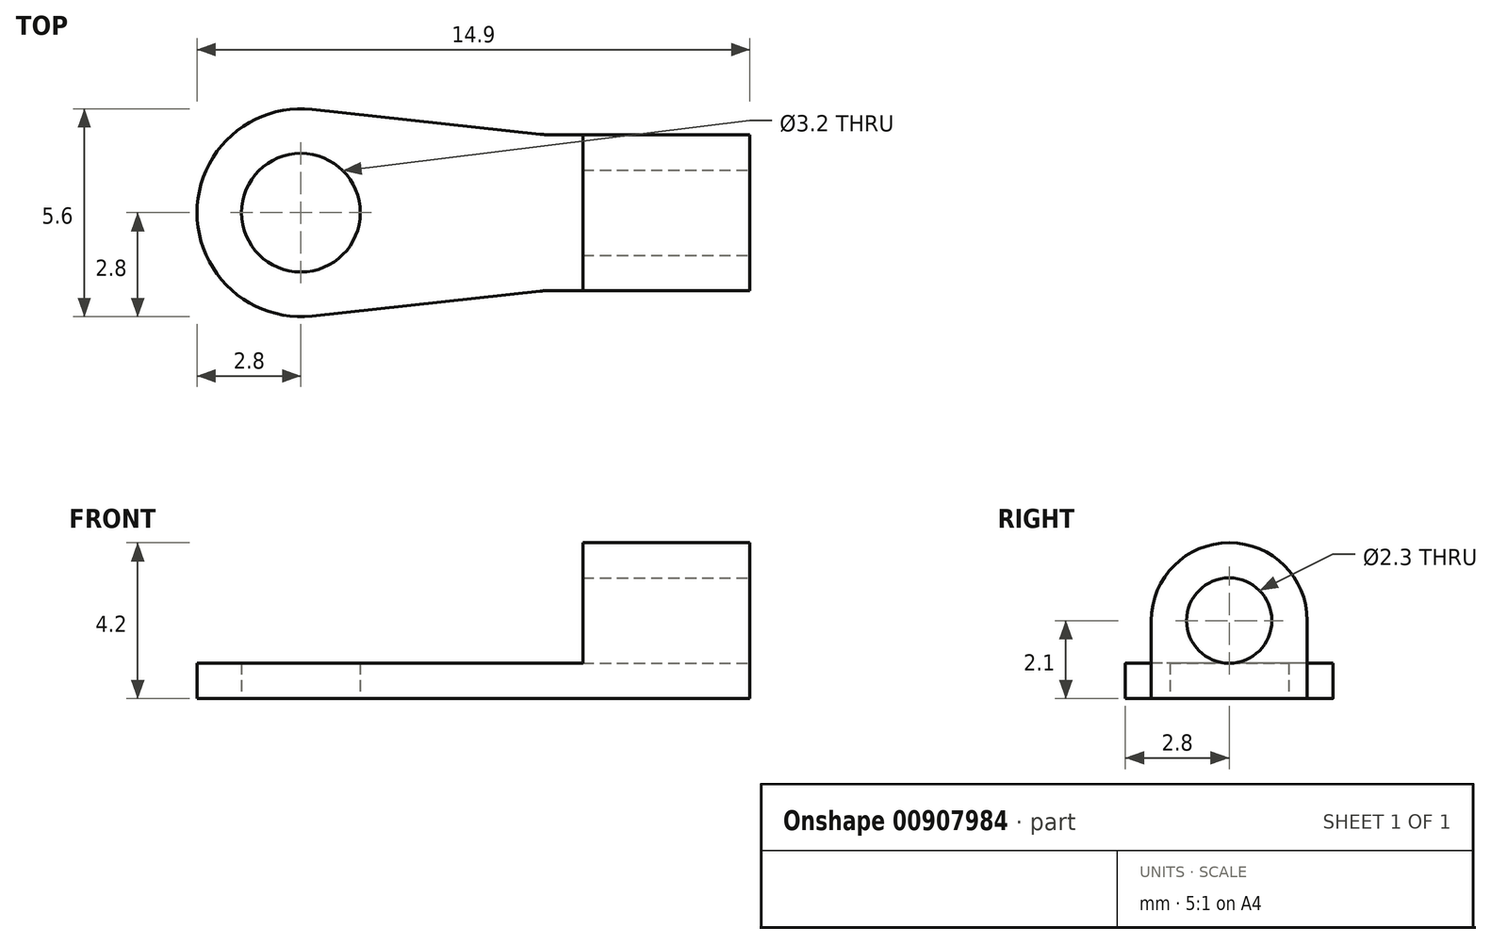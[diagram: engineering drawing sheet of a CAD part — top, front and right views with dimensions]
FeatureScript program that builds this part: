
annotation { "Feature Type Name" : "Feature", "Feature Type Description" : "" }
export const myFeature = defineFeature(function(context is Context, id is Id, definition is map)
    precondition{}
    {
        {
            var Q0;
            Q0=qCreatedBy(makeId("Top.planeOp"),FACE);
            var sketch = newSketch(context, id + "F0", { "sketchPlane" : qUnion([Q0])});
            skLineSegment(sketch, "E0.left", {"start": v(0, 2.8) * mm, "end": v(0, 2.8) * mm});
            skLineSegment(sketch, "E0.right", {"start": v(14.9, 0.7) * mm, "end": v(14.9, 4.9) * mm});
            skPoint(sketch, "E1.visualSharp", {"position": v(0, 5.6) * mm});
            skArc(sketch, "E1.filletArc", {"start": v(2.8, 5.6) * mm, "mid": v(0.82, 4.78) * mm, "end": v(0, 2.8) * mm});
            skPoint(sketch, "E2.visualSharp", {"position": v(0, 0) * mm});
            skArc(sketch, "E2.filletArc", {"start": v(0, 2.8) * mm, "mid": v(0.82, 0.82) * mm, "end": v(2.8, 0) * mm});
            skLineSegment(sketch, "E3.bottom", {"start": v(14.9, 0.7) * mm, "end": v(9.55, 0.7) * mm});
            skLineSegment(sketch, "E3.top", {"start": v(14.9, 4.9) * mm, "end": v(9.55, 4.9) * mm});
            skPoint(sketch, "E3.middle", {"position": v(14.9, 2.8) * mm});
            skArc(sketch, "E4", {"start": v(3.1, 5.58) * mm, "mid": v(0, 2.8) * mm, "end": v(3.1, 0.02) * mm});
            skCircle(sketch, "E5", {"center": v(2.8, 2.8) * mm, "radius": 1.6 * mm});
            skLineSegment(sketch, "E6", {"start": v(9.25, 4.92) * mm, "end": v(3.1, 5.58) * mm});
            skLineSegment(sketch, "E7", {"start": v(9.25, 0.68) * mm, "end": v(3.1, 0.02) * mm});
            skPoint(sketch, "E3.left.end.orphan", {"position": v(19.4, 4.9) * mm});
            skPoint(sketch, "E8.orphan", {"position": v(19.4, 0.7) * mm});
            skPoint(sketch, "E0.bottom.end.orphan", {"position": v(14.9, 0) * mm});
            skPoint(sketch, "E0.top.end.orphan", {"position": v(14.9, 5.6) * mm});
            skPoint(sketch, "E3.right.end.orphan", {"position": v(10.4, 4.9) * mm});
            skPoint(sketch, "E3.right.start.orphan", {"position": v(10.4, 0.7) * mm});
            skPoint(sketch, "E9.visualSharp", {"position": v(9.4, 4.9) * mm});
            skArc(sketch, "E9.filletArc", {"start": v(9.25, 4.92) * mm, "mid": v(9.4, 4.9) * mm, "end": v(9.55, 4.9) * mm});
            skPoint(sketch, "E10.visualSharp", {"position": v(9.4, 0.7) * mm});
            skArc(sketch, "E10.filletArc", {"start": v(9.55, 0.7) * mm, "mid": v(9.4, 0.7) * mm, "end": v(9.25, 0.68) * mm});
            skSolve(sketch);
        }
        {
            var Q0;
            Q0=makeQuery(id+"F0.imprint","IMPRINT",FACE,{"disambiguationData":[TD([[makeQuery(id+"F0.imprint","IMPRINT",EDGE,{"derivedFrom":sQuery(id+"F0.wireOp",EDGE,"E0.right")}),1.0]])]});
            extrude(context, id + "F1", {"entities" : qUnion([Q0]), "depth" : 0.95 * mm, "offsetDistance" : 25 * mm});
        }
        {
            var Q0;
            Q0=makeQuery(id+"F1.opExtrude","CAP_FACE",FACE,{"disambiguationData":[OSD([sQuery(id+"F0.wireOp",EDGE,"E0.right"),sQuery(id+"F0.wireOp",EDGE,"E3.bottom"),sQuery(id+"F0.wireOp",EDGE,"E3.top"),sQuery(id+"F0.wireOp",EDGE,"E4"),sQuery(id+"F0.wireOp",EDGE,"E5"),sQuery(id+"F0.wireOp",EDGE,"E6"),sQuery(id+"F0.wireOp",EDGE,"E7"),sQuery(id+"F0.wireOp",EDGE,"E9.filletArc"),sQuery(id+"F0.wireOp",EDGE,"E10.filletArc")])],"isStart":false});
            var sketch = newSketch(context, id + "F2", { "sketchPlane" : qUnion([Q0])});
            skLineSegment(sketch, "E11.bottom", {"start": v(14.9, 4.9) * mm, "end": v(10.4, 4.9) * mm});
            skLineSegment(sketch, "E11.top", {"start": v(14.9, 0.7) * mm, "end": v(10.4, 0.7) * mm});
            skLineSegment(sketch, "E11.left", {"start": v(14.9, 4.9) * mm, "end": v(14.9, 0.7) * mm});
            skLineSegment(sketch, "E11.right", {"start": v(10.4, 4.9) * mm, "end": v(10.4, 0.7) * mm});
            skSolve(sketch);
        }
        {
            var Q0;
            Q0=makeQuery(id+"F2.imprint","IMPRINT",FACE,{"disambiguationData":[TD([[makeQuery(id+"F2.imprint","IMPRINT",EDGE,{"derivedFrom":sQuery(id+"F2.wireOp",EDGE,"E11.bottom")}),1.0]])]});
            extrude(context, id + "F3", {"entities" : qUnion([Q0]), "operationType" : NewBodyOperationType.ADD, "depth" : 3.25 * mm, "offsetDistance" : 25 * mm});
        }
        {
            var Q0;
            Q0=makeQuery(id+"F3.opExtrude","CAP_EDGE",EDGE,{"disambiguationData":[OSD([sQuery(id+"F2.wireOp",EDGE,"E11.top")])],"isStart":false});
            var Q1;
            Q1=makeQuery(id+"F3.opExtrude","CAP_EDGE",EDGE,{"disambiguationData":[OSD([sQuery(id+"F2.wireOp",EDGE,"E11.bottom")])],"isStart":false});
            fillet(context, id + "F4", {"entities" : qUnion([Q0, Q1]), "radius" : 2.1 * mm, "tangentPropagation" : true, "allowEdgeOverflow" : false});
        }
        {
            var Q0;
            Q0=makeQuery(id+"F3.boolean.opBoolean","MERGE",FACE,{"derivedFrom":[makeQuery(id+"F1.opExtrude","SWEPT_FACE",FACE,{"disambiguationData":[OSD([sQuery(id+"F0.wireOp",EDGE,"E0.right")])]}),makeQuery(id+"F3.opExtrude","SWEPT_FACE",FACE,{"disambiguationData":[OSD([sQuery(id+"F2.wireOp",EDGE,"E11.left")])]})]});
            var sketch = newSketch(context, id + "F5", { "sketchPlane" : qUnion([Q0])});
            skCircle(sketch, "E12", {"center": v(2.8, 2.1) * mm, "radius": 1.15 * mm});
            skSolve(sketch);
        }
        {
            var Q0;
            Q0=makeQuery(id+"F5.imprint","IMPRINT",FACE,{"disambiguationData":[TD([[makeQuery(id+"F5.imprint","IMPRINT",EDGE,{"derivedFrom":sQuery(id+"F5.wireOp",EDGE,"E12")}),1.0]])]});
            extrude(context, id + "F6", {"entities" : qUnion([Q0]), "operationType" : NewBodyOperationType.REMOVE, "oppositeDirection" : true, "depth" : 25 * mm, "offsetDistance" : 25 * mm});
        }
    });
